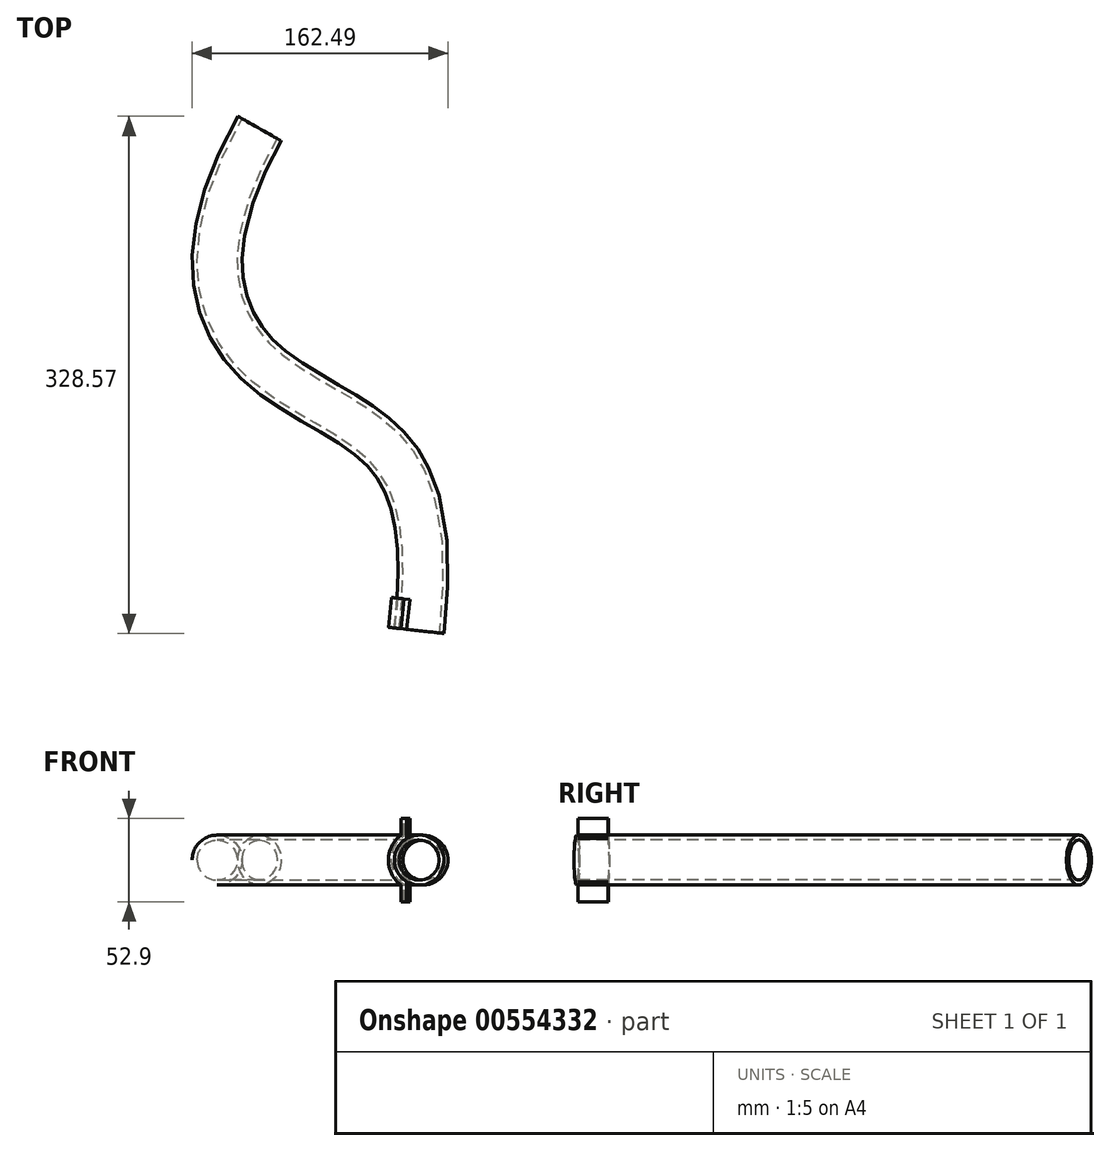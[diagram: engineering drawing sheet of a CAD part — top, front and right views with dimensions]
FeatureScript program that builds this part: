
annotation { "Feature Type Name" : "Feature", "Feature Type Description" : "" }
export const myFeature = defineFeature(function(context is Context, id is Id, definition is map)
    precondition{}
    {
        {
            var Q0;
            Q0=qCreatedBy(makeId("Top.planeOp"),FACE);
            var sketch = newSketch(context, id + "F0", { "sketchPlane" : qUnion([Q0])});
            skFitSpline(sketch, "E0", {"points": [v(81.56, -132.32) * mm, v(62.42, -19.16) * mm, v(-22.23, 40.96) * mm, v(-19.82, 186.6) * mm], "startDerivative": vector(49.33, 442.96) * mm, "endDerivative": vector(324.38, 565.7) * mm});
            skSolve(sketch);
        }
        {
            var Q0;
            Q0=sQuery(id+"F0.wireOp",EDGE,"E0");
            var Q1;
            Q1=sQuery(id+"F0.wireOp",VERTEX,"E0.start");
            cPlane(context, id + "F1", {"entities" : qUnion([Q0, Q1]), "cplaneType" : CPlaneType.CURVE_POINT, "offset" : 25.4 * mm, "width" : 152.4 * mm, "height" : 152.4 * mm});
        }
        {
            var Q0;
            Q0=qCreatedBy(id+"F1.planeOp",FACE);
            var sketch = newSketch(context, id + "F2", { "sketchPlane" : qUnion([Q0])});
            skPoint(sketch, "E1.0", {"position": v(-95.7, 0) * mm});
            skCircle(sketch, "E2", {"center": v(-95.7, 0) * mm, "radius": 12.7 * mm});
            skLineSegment(sketch, "E3", {"start": v(-87.76, -26.45) * mm, "end": v(-87.76, -13.75) * mm});
            skLineSegment(sketch, "E4.trimOffspring", {"start": v(-87.76, 13.75) * mm, "end": v(-87.76, 26.45) * mm});
            skArc(sketch, "E5", {"start": v(-87.76, 13.75) * mm, "mid": v(-111.58, 0) * mm, "end": v(-87.76, -13.75) * mm});
            skArc(sketch, "E6", {"start": v(-87.76, -13.75) * mm, "mid": v(-79.83, 0) * mm, "end": v(-87.76, 13.75) * mm});
            skLineSegment(sketch, "E7", {"start": v(-95.7, 0) * mm, "end": v(-79.83, 0) * mm, "construction": true});
            skLineSegment(sketch, "E8", {"start": v(-95.7, 0) * mm, "end": v(-87.76, 13.75) * mm, "construction": true});
            skLineSegment(sketch, "E9.0", {"start": v(-83.95, 15.8) * mm, "end": v(-83.95, 26.45) * mm});
            skArc(sketch, "E10.0", {"start": v(-83.95, -15.8) * mm, "mid": v(-76.02, 0) * mm, "end": v(-83.95, 15.8) * mm});
            skLineSegment(sketch, "E10.1", {"start": v(-83.95, -26.45) * mm, "end": v(-83.95, -15.8) * mm});
            skLineSegment(sketch, "E11", {"start": v(-83.95, 26.45) * mm, "end": v(-87.76, 26.45) * mm});
            skLineSegment(sketch, "E12", {"start": v(-83.95, -26.45) * mm, "end": v(-87.76, -26.45) * mm});
            skSolve(sketch);
        }
        {
            var Q0;
            Q0=makeQuery(id+"F2.imprint","IMPRINT",FACE,{"disambiguationData":[TD([[makeQuery(id+"F2.imprint","IMPRINT",EDGE,{"derivedFrom":sQuery(id+"F2.wireOp",EDGE,"E2")}),-1.0]])]});
            var Q1;
            Q1=sQuery(id+"F0.wireOp",EDGE,"E0");
            sweep(context, id + "F3", {"profiles" : qUnion([Q0]), "path" : qUnion([Q1])});
        }
        {
            var Q0;
            Q0=makeQuery(id+"F2.imprint","IMPRINT",FACE,{"disambiguationData":[TD([[makeQuery(id+"F2.imprint","IMPRINT",EDGE,{"derivedFrom":sQuery(id+"F2.wireOp",EDGE,"E3")}),-1.0]])]});
            extrude(context, id + "F4", {"entities" : qUnion([Q0]), "depth" : 19.05 * mm, "offsetDistance" : 25.4 * mm});
        }
    });
